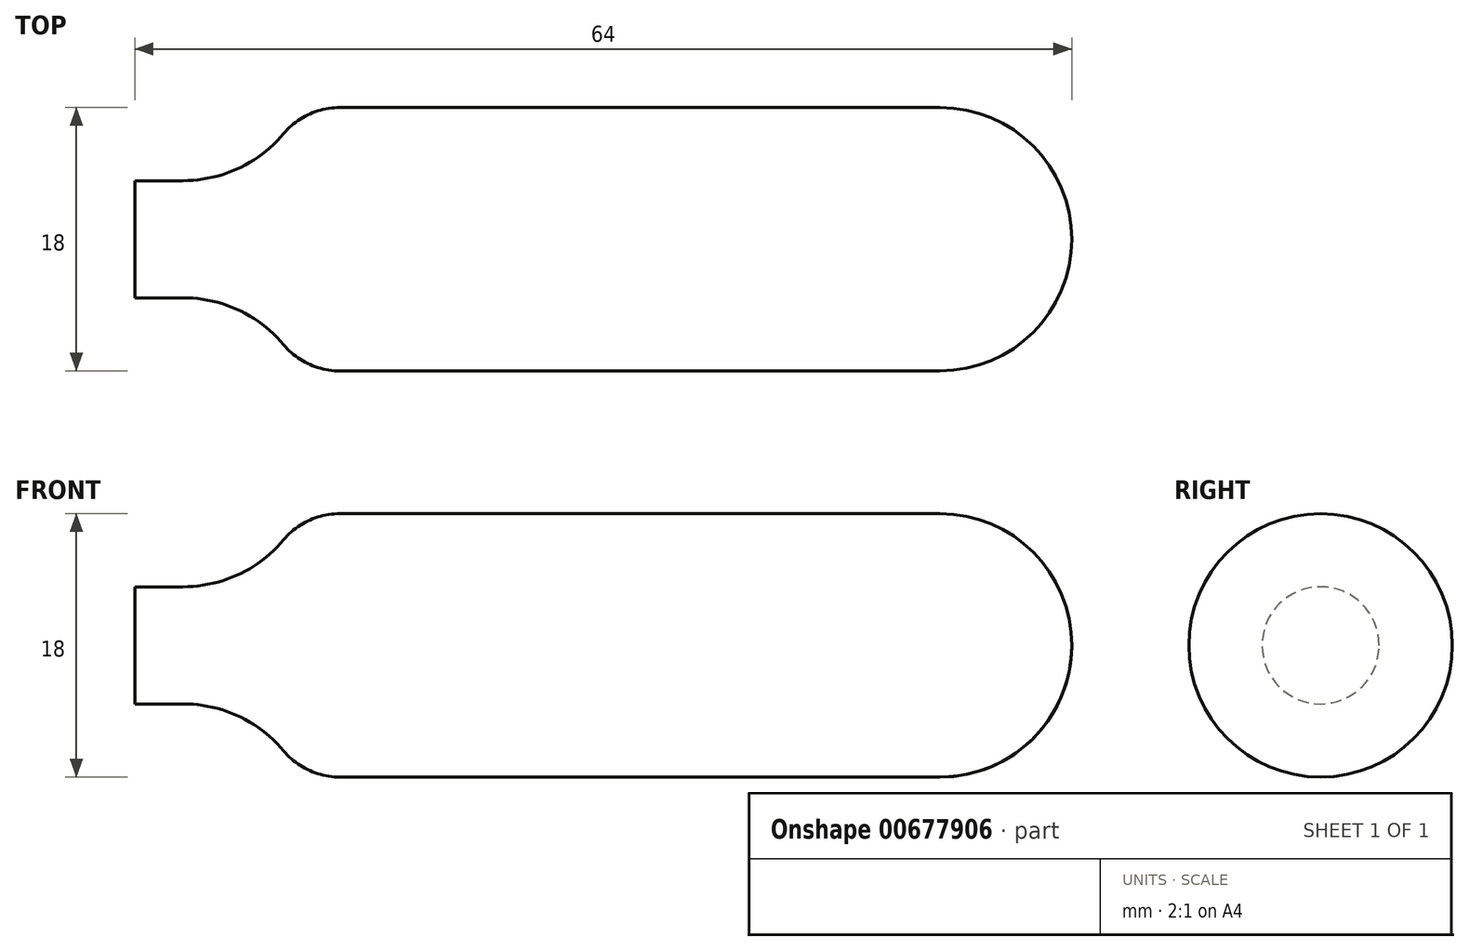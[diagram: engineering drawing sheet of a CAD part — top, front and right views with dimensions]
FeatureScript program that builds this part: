
annotation { "Feature Type Name" : "Feature", "Feature Type Description" : "" }
export const myFeature = defineFeature(function(context is Context, id is Id, definition is map)
    precondition{}
    {
        {
            var Q0;
            Q0=qCreatedBy(makeId("Front.planeOp"),FACE);
            var sketch = newSketch(context, id + "F0", { "sketchPlane" : qUnion([Q0])});
            skLineSegment(sketch, "E0", {"start": v(0, 0) * mm, "end": v(0, 4) * mm});
            skLineSegment(sketch, "E1", {"start": v(0, 4) * mm, "end": v(9, 4) * mm});
            skLineSegment(sketch, "E2", {"start": v(9, 4) * mm, "end": v(9, 9) * mm});
            skLineSegment(sketch, "E3", {"start": v(9, 9) * mm, "end": v(64, 9) * mm});
            skLineSegment(sketch, "E4", {"start": v(64, 9) * mm, "end": v(64, 0) * mm});
            skLineSegment(sketch, "E5", {"start": v(0, 0) * mm, "end": v(64, 0) * mm});
            skSolve(sketch);
        }
        {
            var Q0;
            Q0=makeQuery(id+"F0.imprint","IMPRINT",FACE,{"disambiguationData":[TD([[makeQuery(id+"F0.imprint","IMPRINT",EDGE,{"derivedFrom":sQuery(id+"F0.wireOp",EDGE,"E0")}),-1.0]])]});
            var Q1;
            Q1=sQuery(id+"F0.wireOp",EDGE,"E5");
            revolve(context, id + "F1", {"entities" : qUnion([Q0]), "axis" : qUnion([Q1]), "revolveType" : RevolveType.FULL});
        }
        {
            var Q0;
            Q0=makeQuery(id+"F1.opRevolve","SWEPT_EDGE",EDGE,{"disambiguationData":[OSD([sQuery(id+"F0.wireOp",EDGE,"E3"),sQuery(id+"F0.wireOp",EDGE,"E4")])]});
            fillet(context, id + "F2", {"entities" : qUnion([Q0]), "radius" : 9 * mm, "tangentPropagation" : true, "allowEdgeOverflow" : false});
        }
        {
            var Q0;
            Q0=makeQuery(id+"F1.opRevolve","SWEPT_EDGE",EDGE,{"disambiguationData":[OSD([sQuery(id+"F0.wireOp",EDGE,"E2"),sQuery(id+"F0.wireOp",EDGE,"E3")])]});
            fillet(context, id + "F3", {"entities" : qUnion([Q0]), "radius" : 5 * mm, "tangentPropagation" : true, "allowEdgeOverflow" : false});
        }
        {
            var Q0;
            Q0=makeQuery(id+"F3.opFillet","BLEND_EDGE",EDGE,{"blendedFrom":[makeQuery(id+"F1.opRevolve","SWEPT_EDGE",EDGE,{"disambiguationData":[OSD([sQuery(id+"F0.wireOp",EDGE,"E2"),sQuery(id+"F0.wireOp",EDGE,"E3")])]}),makeQuery(id+"F1.opRevolve","SWEPT_FACE",FACE,{"disambiguationData":[OSD([sQuery(id+"F0.wireOp",EDGE,"E1")])]})],"blendedInto":[makeQuery(id+"F1.opRevolve","SWEPT_FACE",FACE,{"disambiguationData":[OSD([sQuery(id+"F0.wireOp",EDGE,"E1")])]})]});
            fillet(context, id + "F4", {"entities" : qUnion([Q0]), "radius" : 9 * mm, "tangentPropagation" : true, "allowEdgeOverflow" : false});
        }
    });
